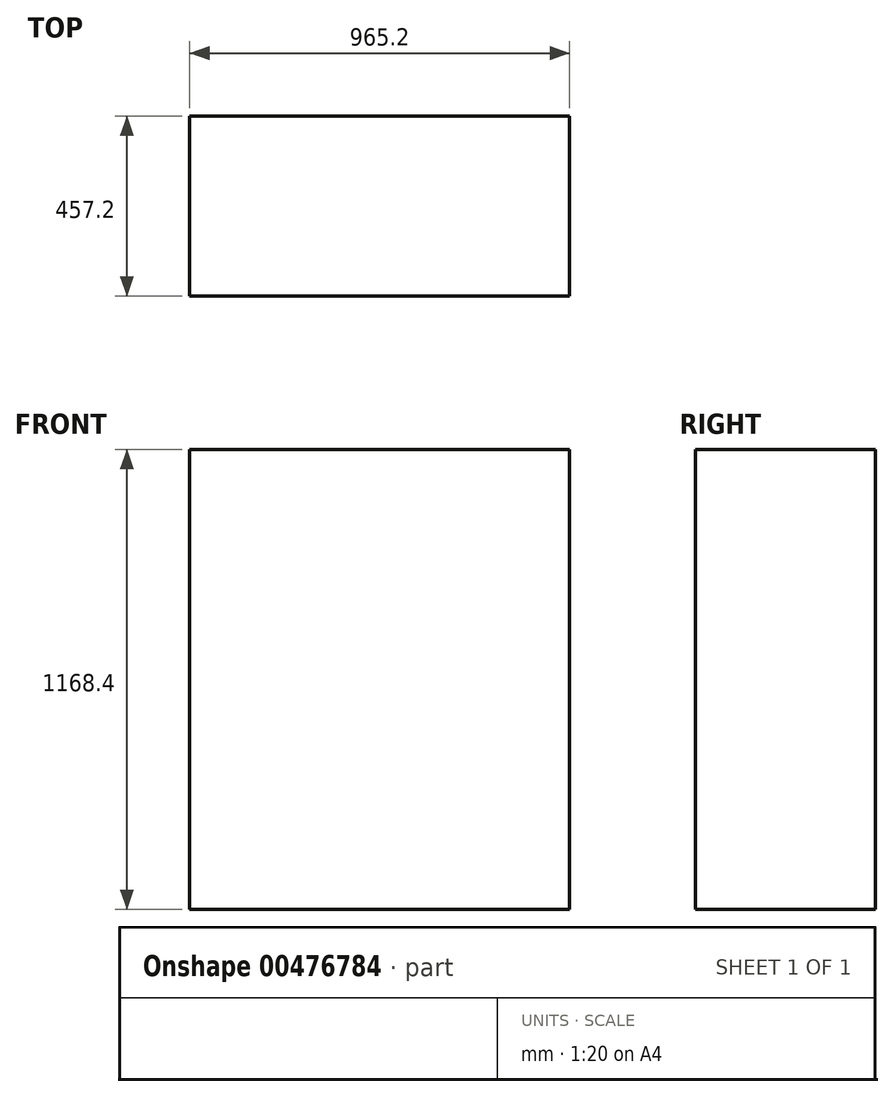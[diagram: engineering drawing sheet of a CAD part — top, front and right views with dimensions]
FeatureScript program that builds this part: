
annotation { "Feature Type Name" : "Feature", "Feature Type Description" : "" }
export const myFeature = defineFeature(function(context is Context, id is Id, definition is map)
    precondition{}
    {
        {
            var Q0;
            Q0=qCreatedBy(makeId("Top.planeOp"),FACE);
            var sketch = newSketch(context, id + "F0", { "sketchPlane" : qUnion([Q0])});
            skLineSegment(sketch, "E0.bottom", {"start": v(0, 0) * mm, "end": v(965.2, 0) * mm});
            skLineSegment(sketch, "E0.top", {"start": v(0, 457.2) * mm, "end": v(965.2, 457.2) * mm});
            skLineSegment(sketch, "E0.left", {"start": v(0, 0) * mm, "end": v(0, 457.2) * mm});
            skLineSegment(sketch, "E0.right", {"start": v(965.2, 0) * mm, "end": v(965.2, 457.2) * mm});
            skSolve(sketch);
        }
        {
            var Q0;
            Q0=qSketchRegion(id+"F0",true);
            extrude(context, id + "F1", {"entities" : qUnion([Q0]), "depth" : 1168.4 * mm});
        }
    });
